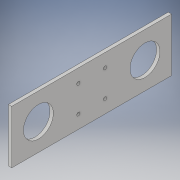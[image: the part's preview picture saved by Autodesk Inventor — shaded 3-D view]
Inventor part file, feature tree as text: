
AUTODESK INVENTOR PART (.ipt)
format: ipt  version: 2017 (Build 210142000, 142)  size: 113,152 bytes
history: native  units: in
note: dims shown in document units (in); Inventor stores cm internally (conversion verified against a paired STEP export)
features: extrude x1, sketch x1
ambient origin geometry x8: Origin, YZ Plane, XZ Plane, XY Plane, X Axis, Y Axis, Z Axis, Center Point
bodies: Body1 (feature_tree)
feature tree (2):
  extrude  "Extrusion2"  Depth=6.0in
  sketch  "Sketch1"  dims[d11=2.0in d12=6.0in d13=1.0in d14=1.125in d22=0.5in d23=0.5in d24=0.125in d25=0.125in d26=0.0in]
